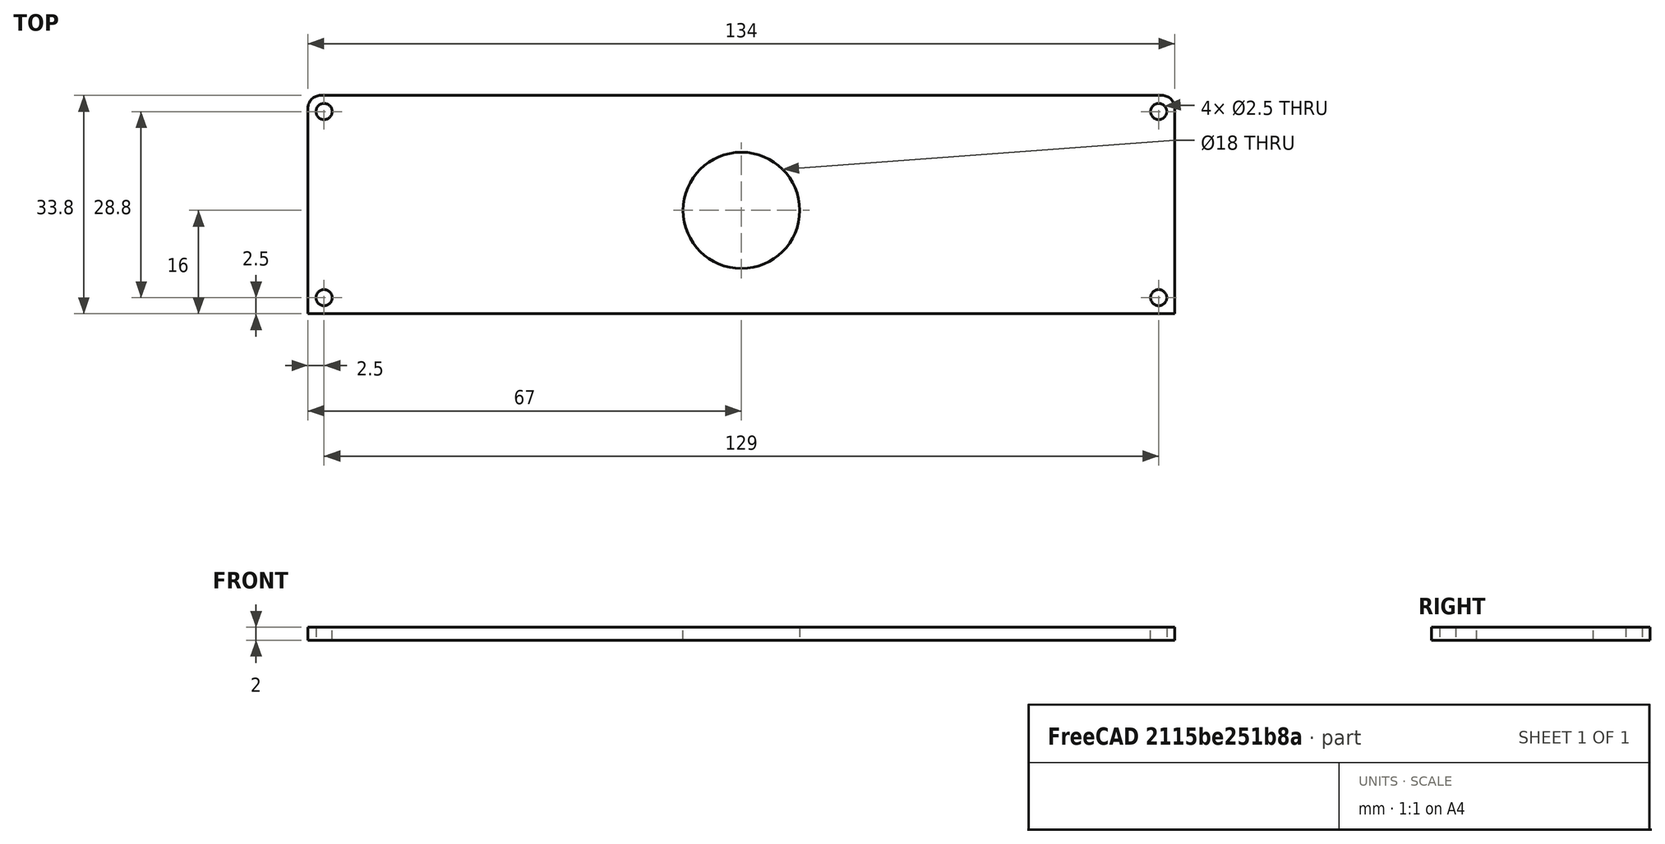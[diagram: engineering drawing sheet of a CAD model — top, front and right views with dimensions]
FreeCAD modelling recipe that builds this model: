
FCSTD DOCUMENT  (FreeCAD 0.18.4R)
Label: 接线盒前板
License: All rights reserved
LicenseURL: http://en.wikipedia.org/wiki/All_rights_reserved
objects: Sketcher::SketchObject×3, TechDraw::DrawViewDimension×3, PartDesign::Pocket×2, PartDesign::Mirrored×2, PartDesign::Pad×1, PartDesign::Fillet×1, TechDraw::DrawSVGTemplate×1, PartDesign::PolarPattern×1, PartDesign::Body×1, TechDraw::DrawViewPart×1, TechDraw::DrawPage×1
note: 14 computed .brp shape members not serialized (recipe doc carries the construction recipe); baked Part::Feature solids carry a one-line shape summary decoded from their .brp

FEATURE [Sketcher::SketchObject] Sketch
  MapMode = 5
  Support = -> [XY_Plane]
  sketch-geometry (4):
    g0: LineSegment StartX=-67 StartY=16.9 StartZ=0 EndX=67 EndY=16.9 EndZ=0
    g1: LineSegment StartX=67 StartY=16.9 StartZ=0 EndX=67 EndY=-16.9 EndZ=0
    g2: LineSegment StartX=67 StartY=-16.9 StartZ=0 EndX=-67 EndY=-16.9 EndZ=0
    g3: LineSegment StartX=-67 StartY=-16.9 StartZ=0 EndX=-67 EndY=16.9 EndZ=0
  constraints (11):
    c: Coincident(g0,g1)
    c: Coincident(g1,g2)
    c: Coincident(g2,g3)
    c: Coincident(g3,g0)
    c: Horizontal(g0)
    c: Horizontal(g2)
    c: Vertical(g1)
    c: Vertical(g3)
    c: DistanceY(g1,g1) = 33.8
    c: DistanceX(g2,g2) = 134
    c: Symmetric(g0,g1,g-1)
FEATURE [PartDesign::Pad] Pad
  Length = 2
  Length2 = 100
  Profile = -> Sketch
  Type = 0
FEATURE [Sketcher::SketchObject] Sketch001
  ExternalGeometry = -> [Pad]
  MapMode = 5
  Placement = pos=(0,0,2) rot=(0,0,1;0rad)
  Support = -> [Pad]
  sketch-geometry (2):
    g0: Circle CenterX=0 CenterY=-0.9 CenterZ=0 NormalX=0 NormalY=0 NormalZ=1 AngleXU=0 Radius=9
    g1: LineSegment [constr] StartX=0 StartY=-0.9 StartZ=0 EndX=0 EndY=-16.9 EndZ=0
  constraints (6):
    c: Diameter(g0) = 18
    c: PointOnObject(g1,g-3)
    c: Coincident(g1,g0)
    c: Vertical(g1)
    c: DistanceY(g1,g1) = 16
    c: PointOnObject(g0,g-2)
FEATURE [PartDesign::Pocket] Pocket
  BaseFeature = -> Pad
  Length = 5
  Length2 = 100
  Profile = -> Sketch001
  Type = 1
FEATURE [PartDesign::Fillet] Fillet
  Base = -> Pocket [Edge1,Edge2]
  BaseFeature = -> Pocket
  Radius = 2
FEATURE [TechDraw::DrawSVGTemplate] Template
  EditableTexts = Designed_by_Name=岳晓凯; FC-Date=2020/11/15; FC-Title=Title; Subtitle=接线盒前板
  Height = 210
  Orientation = 1
  Width = 297
FEATURE [Sketcher::SketchObject] Sketch002
  ExternalGeometry = -> [Fillet]
  MapMode = 5
  Support = -> [XY_Plane]
  sketch-geometry (3):
    g0: Circle CenterX=-64.5 CenterY=-14.4 CenterZ=0 NormalX=0 NormalY=0 NormalZ=1 AngleXU=0 Radius=1.25
    g1: LineSegment [constr] StartX=-64.5 StartY=-14.4 StartZ=0 EndX=-64.5 EndY=-16.9 EndZ=0
    g2: LineSegment [constr] StartX=-64.5 StartY=-14.4 StartZ=0 EndX=-67 EndY=-14.4 EndZ=0
  constraints (9):
    c: Diameter(g0) = 2.5
    c: PointOnObject(g2,g-4)
    c: PointOnObject(g1,g-5)
    c: Coincident(g1,g2)
    c: Coincident(g0,g1)
    c: Horizontal(g2)
    c: Vertical(g1)
    c: DistanceX(g2,g2) = 2.5
    c: DistanceY(g1,g1) = 2.5
FEATURE [PartDesign::Pocket] Pocket001
  BaseFeature = -> Fillet
  Length = 5
  Length2 = 100
  Profile = -> Sketch002
  Reversed = true
  Type = 1
FEATURE [PartDesign::Mirrored] Mirrored
  BaseFeature = -> Pocket001
  MirrorPlane = -> YZ_Plane
  Originals = -> [Pocket001]
FEATURE [PartDesign::Mirrored] Mirrored001
  BaseFeature = -> Mirrored
  MirrorPlane = -> XZ_Plane
  Originals = -> [Pocket001]
FEATURE [PartDesign::PolarPattern] PolarPattern
  Angle = 360
  Axis = -> Sketch002 [N_Axis]
  BaseFeature = -> Mirrored001
  Occurrences = 2
  Originals = -> [Pocket001]
FEATURE [PartDesign::Body] Body
  Group = -> [Sketch,Pad,Sketch001,Pocket,Fillet,Sketch002,Pocket001,Mirrored,Mirrored001,PolarPattern]
  Origin = -> Origin
  Tip = -> PolarPattern
FEATURE [TechDraw::DrawViewPart] View
  CoarseView = false
  Direction = (0,0,1)
  Focus = 100
  HardHidden = false
  IsoCount = 0
  IsoHidden = false
  IsoVisible = false
  LockPosition = false
  Perspective = false
  Rotation = 0
  ScaleType = 0
  SeamHidden = false
  SeamVisible = false
  SmoothHidden = false
  SmoothVisible = false
  Source = -> [Body]
  X = 144.027
  Y = 141.02
FEATURE [TechDraw::DrawViewDimension] Dimension001
  Arbitrary = false
  FormatSpec = %.2f
  LockPosition = false
  MeasureType = 1
  OverTolerance = 0
  References2D = -> [View]
  Rotation = 0
  ScaleType = 0
  Type = 1
  UnderTolerance = 0
  X = -29.8215
  Y = -21.745
FEATURE [TechDraw::DrawViewDimension] Dimension
  Arbitrary = false
  FormatSpec = ⌀%.2f
  LockPosition = false
  MeasureType = 1
  OverTolerance = 0
  References2D = -> [View]
  Rotation = 0
  ScaleType = 0
  Type = 5
  UnderTolerance = 0
  X = 33.3793
  Y = 10.8994
FEATURE [TechDraw::DrawViewDimension] Dimension002
  Arbitrary = false
  FormatSpec = %.2f
  LockPosition = false
  MeasureType = 1
  OverTolerance = 0
  References2D = -> [View]
  Rotation = 0
  ScaleType = 0
  Type = 2
  UnderTolerance = 0
  X = -78.2029
  Y = -7.94631
FEATURE [TechDraw::DrawPage] Page
  KeepUpdated = true
  ProjectionType = 0
  Template = -> Template
  Views = -> [View,Dimension,Dimension001,Dimension002]
